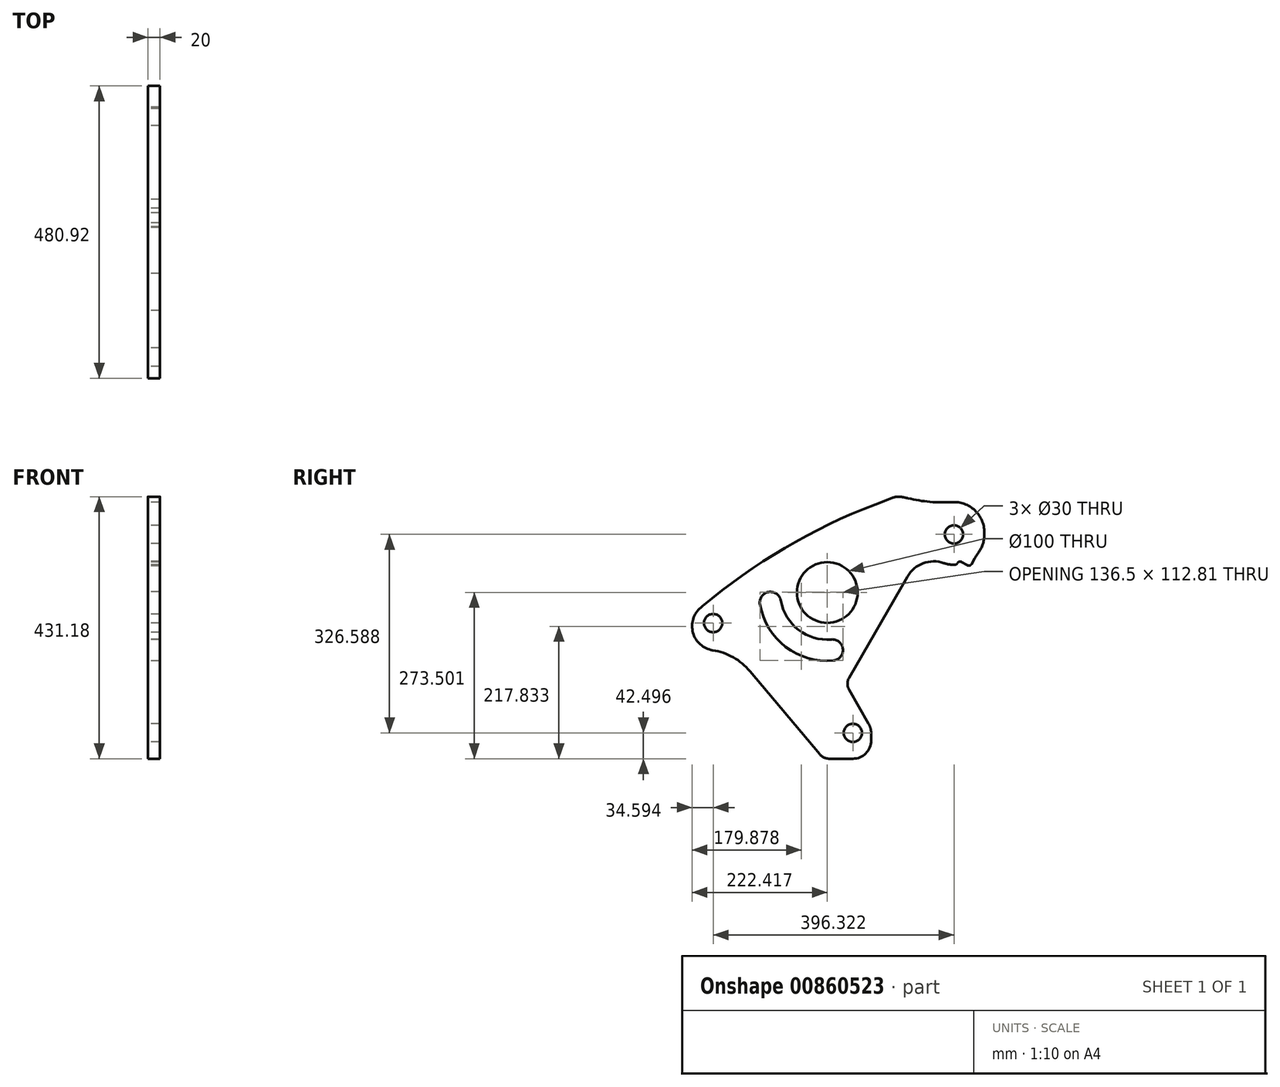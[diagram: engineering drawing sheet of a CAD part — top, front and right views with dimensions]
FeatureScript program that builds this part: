
annotation { "Feature Type Name" : "Feature", "Feature Type Description" : "" }
export const myFeature = defineFeature(function(context is Context, id is Id, definition is map)
    precondition{}
    {
        {
            var Q0;
            Q0=qCreatedBy(makeId("Right.planeOp"),FACE);
            var sketch = newSketch(context, id + "F0", { "sketchPlane" : qUnion([Q0])});
            skArc(sketch, "E0", {"start": v(-12.88, 3.84) * mm, "mid": v(-11.46, 5.86) * mm, "end": v(-9.44, 4.45) * mm});
            skArc(sketch, "E1", {"start": v(-9.44, 4.45) * mm, "mid": v(-6.52, -0.36) * mm, "end": v(-1.13, -1.93) * mm});
            skArc(sketch, "E2", {"start": v(-1.13, -1.93) * mm, "mid": v(0.77, -3.52) * mm, "end": v(-0.82, -5.42) * mm});
            skArc(sketch, "E3", {"start": v(-0.82, -5.42) * mm, "mid": v(-8.65, -3.13) * mm, "end": v(-12.88, 3.84) * mm});
            skCircle(sketch, "E4", {"center": v(-1.8, 5.8) * mm, "radius": 5 * mm});
            skCircle(sketch, "E5", {"center": v(2.4, -17.3) * mm, "radius": 1.5 * mm});
            skCircle(sketch, "E6", {"center": v(19.05, 15.35) * mm, "radius": 1.5 * mm});
            skCircle(sketch, "E7", {"center": v(-20.59, 0.76) * mm, "radius": 1.5 * mm});
            skArc(sketch, "E8", {"start": v(21.21, 10.27) * mm, "mid": v(21.6, 10.22) * mm, "end": v(21.9, 10.45) * mm});
            skLineSegment(sketch, "E9", {"start": v(21.9, 10.45) * mm, "end": v(22.43, 11.35) * mm});
            skArc(sketch, "E10", {"start": v(22.43, 11.35) * mm, "mid": v(22.8, 11.94) * mm, "end": v(23.17, 12.53) * mm});
            skArc(sketch, "E11", {"start": v(23.17, 12.53) * mm, "mid": v(23.82, 13.87) * mm, "end": v(24.05, 15.35) * mm});
            skLineSegment(sketch, "E12", {"start": v(24.05, 15.35) * mm, "end": v(24.05, 15.68) * mm});
            skArc(sketch, "E13", {"start": v(24.05, 15.68) * mm, "mid": v(22.47, 19.32) * mm, "end": v(18.74, 20.67) * mm});
            skArc(sketch, "E14", {"start": v(18.74, 20.67) * mm, "mid": v(15.1, 20.71) * mm, "end": v(11.5, 21.29) * mm});
            skArc(sketch, "E15", {"start": v(11.5, 21.29) * mm, "mid": v(11.03, 21.4) * mm, "end": v(10.56, 21.5) * mm});
            skArc(sketch, "E16", {"start": v(10.56, 21.5) * mm, "mid": v(9.7, 21.55) * mm, "end": v(8.87, 21.36) * mm});
            skLineSegment(sketch, "E17", {"start": v(8.87, 21.36) * mm, "end": v(6.1, 20.3) * mm});
            skArc(sketch, "E18", {"start": v(6.1, 20.3) * mm, "mid": v(-8.81, 13.1) * mm, "end": v(-22.34, 3.54) * mm});
            skLineSegment(sketch, "E19", {"start": v(-22.34, 3.54) * mm, "end": v(-22.62, 3.31) * mm});
            skArc(sketch, "E20", {"start": v(-22.62, 3.31) * mm, "mid": v(-23.9, -0.83) * mm, "end": v(-20.65, -3.7) * mm});
            skArc(sketch, "E21", {"start": v(-20.65, -3.7) * mm, "mid": v(-17.27, -4.88) * mm, "end": v(-14.52, -7.16) * mm});
            skLineSegment(sketch, "E22", {"start": v(-14.52, -7.16) * mm, "end": v(-3.03, -20.84) * mm});
            skArc(sketch, "E23", {"start": v(-3.03, -20.84) * mm, "mid": v(-2.35, -21.37) * mm, "end": v(-1.5, -21.56) * mm});
            skLineSegment(sketch, "E24", {"start": v(-1.5, -21.56) * mm, "end": v(2.4, -21.56) * mm});
            skArc(sketch, "E25", {"start": v(2.4, -21.56) * mm, "mid": v(4.53, -20.68) * mm, "end": v(5.4, -18.56) * mm});
            skLineSegment(sketch, "E26", {"start": v(5.4, -18.56) * mm, "end": v(5.4, -17.3) * mm});
            skArc(sketch, "E27", {"start": v(5.4, -17.3) * mm, "mid": v(5.3, -16.53) * mm, "end": v(5, -15.8) * mm});
            skLineSegment(sketch, "E28", {"start": v(5, -15.8) * mm, "end": v(1.78, -10.23) * mm});
            skArc(sketch, "E29", {"start": v(1.78, -10.23) * mm, "mid": v(1.51, -9.23) * mm, "end": v(1.78, -8.23) * mm});
            skLineSegment(sketch, "E30", {"start": v(1.78, -8.23) * mm, "end": v(11.4, 8.42) * mm});
            skArc(sketch, "E31", {"start": v(11.4, 8.42) * mm, "mid": v(13.99, 10.6) * mm, "end": v(17.38, 10.63) * mm});
            skArc(sketch, "E32", {"start": v(17.38, 10.63) * mm, "mid": v(18.27, 10.4) * mm, "end": v(19.18, 10.35) * mm});
            skArc(sketch, "E33", {"start": v(19.18, 10.35) * mm, "mid": v(19.43, 10.43) * mm, "end": v(19.61, 10.62) * mm});
            skArc(sketch, "E34", {"start": v(19.61, 10.62) * mm, "mid": v(19.92, 10.86) * mm, "end": v(20.3, 10.82) * mm});
            skLineSegment(sketch, "E35", {"start": v(20.3, 10.82) * mm, "end": v(21.21, 10.27) * mm});
            skSolve(sketch);
        }
        {
            var Q0;
            Q0 = qSketchRegion(id + "F0", true);
            extrude(context, id + "F1", {"entities" : qUnion([Q0]), "depth" : 2 * mm, "offsetDistance" : 25 * mm});
        }
        {
            var Q0;
            Q0=makeQuery(id+"F1.opExtrude","SWEPT_BODY",BODY,{"disambiguationData":[OSD([sQuery(id+"F0.wireOp",EDGE,"E0"),sQuery(id+"F0.wireOp",EDGE,"E1"),sQuery(id+"F0.wireOp",EDGE,"E2"),sQuery(id+"F0.wireOp",EDGE,"E3"),sQuery(id+"F0.wireOp",EDGE,"E4"),sQuery(id+"F0.wireOp",EDGE,"E5"),sQuery(id+"F0.wireOp",EDGE,"E6"),sQuery(id+"F0.wireOp",EDGE,"E7"),sQuery(id+"F0.wireOp",EDGE,"E8"),sQuery(id+"F0.wireOp",EDGE,"E9"),sQuery(id+"F0.wireOp",EDGE,"E10"),sQuery(id+"F0.wireOp",EDGE,"E11"),sQuery(id+"F0.wireOp",EDGE,"E12"),sQuery(id+"F0.wireOp",EDGE,"E13"),sQuery(id+"F0.wireOp",EDGE,"E14"),sQuery(id+"F0.wireOp",EDGE,"E15"),sQuery(id+"F0.wireOp",EDGE,"E16"),sQuery(id+"F0.wireOp",EDGE,"E17"),sQuery(id+"F0.wireOp",EDGE,"E18"),sQuery(id+"F0.wireOp",EDGE,"E19"),sQuery(id+"F0.wireOp",EDGE,"E20"),sQuery(id+"F0.wireOp",EDGE,"E21"),sQuery(id+"F0.wireOp",EDGE,"E22"),sQuery(id+"F0.wireOp",EDGE,"E23"),sQuery(id+"F0.wireOp",EDGE,"E24"),sQuery(id+"F0.wireOp",EDGE,"E25"),sQuery(id+"F0.wireOp",EDGE,"E26"),sQuery(id+"F0.wireOp",EDGE,"E27"),sQuery(id+"F0.wireOp",EDGE,"E28"),sQuery(id+"F0.wireOp",EDGE,"E29"),sQuery(id+"F0.wireOp",EDGE,"E30"),sQuery(id+"F0.wireOp",EDGE,"E31"),sQuery(id+"F0.wireOp",EDGE,"E32"),sQuery(id+"F0.wireOp",EDGE,"E33"),sQuery(id+"F0.wireOp",EDGE,"E34"),sQuery(id+"F0.wireOp",EDGE,"E35")])]});
            var Q1;
            Q1=sQuery(id+"F0.wireOp",VERTEX,"E7.center");
            transform(context, id + "F2", {"entities" : qUnion([Q0]), "transformType" : TransformType.SCALE_UNIFORMLY, "scale" : 10, "scalePoint" : qUnion([Q1]), "makeCopy" : false});
        }
    });
